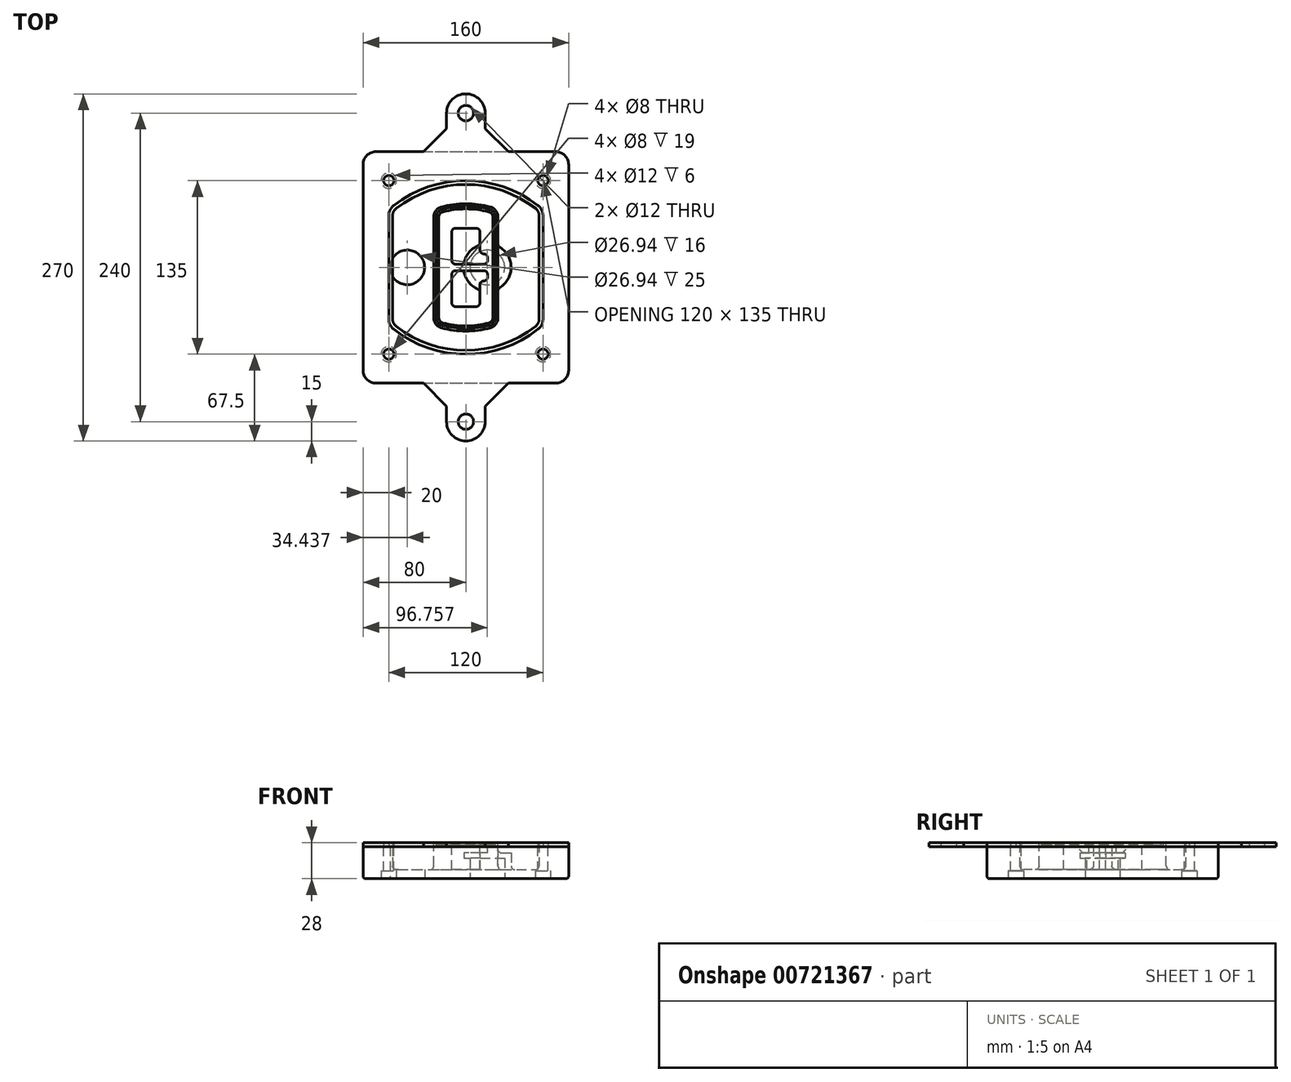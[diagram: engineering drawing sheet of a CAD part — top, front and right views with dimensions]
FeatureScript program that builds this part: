
annotation { "Feature Type Name" : "Feature", "Feature Type Description" : "" }
export const myFeature = defineFeature(function(context is Context, id is Id, definition is map)
    precondition{}
    {
        {
            var Q0;
            Q0=qCreatedBy(makeId("Top.planeOp"),FACE);
            var sketch = newSketch(context, id + "F0", { "sketchPlane" : qUnion([Q0])});
            skPoint(sketch, "E0.rect.middle", {"position": v(0, 0) * mm});
            skLineSegment(sketch, "E1.bottom", {"start": v(-70, -90) * mm, "end": v(70, -90) * mm});
            skLineSegment(sketch, "E1.top", {"start": v(-70, 90) * mm, "end": v(70, 90) * mm});
            skLineSegment(sketch, "E1.left", {"start": v(-80, -80) * mm, "end": v(-80, 80) * mm});
            skLineSegment(sketch, "E1.right", {"start": v(80, -80) * mm, "end": v(80, 80) * mm});
            skLineSegment(sketch, "E2", {"start": v(-80, 90) * mm, "end": v(80, -90) * mm, "construction": true});
            skLineSegment(sketch, "E3", {"start": v(80, 90) * mm, "end": v(-80, -90) * mm, "construction": true});
            skCircle(sketch, "E4", {"center": v(-60, 67.5) * mm, "radius": 4 * mm});
            skCircle(sketch, "E5", {"center": v(60, 67.5) * mm, "radius": 4 * mm});
            skCircle(sketch, "E6", {"center": v(60, -67.5) * mm, "radius": 4 * mm});
            skCircle(sketch, "E7", {"center": v(-60, -67.5) * mm, "radius": 4 * mm});
            skLineSegment(sketch, "E8", {"start": v(-60, 67.5) * mm, "end": v(60, 67.5) * mm, "construction": true});
            skLineSegment(sketch, "E9", {"start": v(60, 67.5) * mm, "end": v(60, -67.5) * mm, "construction": true});
            skLineSegment(sketch, "E10", {"start": v(60, -67.5) * mm, "end": v(-60, -67.5) * mm, "construction": true});
            skLineSegment(sketch, "E11", {"start": v(-60, -67.5) * mm, "end": v(-60, 67.5) * mm, "construction": true});
            skLineSegment(sketch, "E12", {"start": v(-60, 40.3) * mm, "end": v(-60, -40.3) * mm});
            skLineSegment(sketch, "E13", {"start": v(60, 40.3) * mm, "end": v(60, -40.3) * mm});
            skArc(sketch, "E14", {"start": v(56.15, 48.18) * mm, "mid": v(0, 67.5) * mm, "end": v(-56.15, 48.18) * mm});
            skArc(sketch, "E15", {"start": v(-56.15, -48.18) * mm, "mid": v(0, -67.5) * mm, "end": v(56.15, -48.18) * mm});
            skLineSegment(sketch, "E16", {"start": v(-60, 0) * mm, "end": v(60, 0) * mm, "construction": true});
            skPoint(sketch, "E17.visualSharp", {"position": v(-60, -45) * mm});
            skArc(sketch, "E17.filletArc", {"start": v(-60, -40.3) * mm, "mid": v(-58.99, -44.68) * mm, "end": v(-56.15, -48.18) * mm});
            skPoint(sketch, "E18.visualSharp", {"position": v(-60, 45) * mm});
            skArc(sketch, "E18.filletArc", {"start": v(-56.15, 48.18) * mm, "mid": v(-58.99, 44.68) * mm, "end": v(-60, 40.3) * mm});
            skPoint(sketch, "E19.visualSharp", {"position": v(60, 45) * mm});
            skArc(sketch, "E19.filletArc", {"start": v(60, 40.3) * mm, "mid": v(58.99, 44.68) * mm, "end": v(56.15, 48.18) * mm});
            skPoint(sketch, "E20.visualSharp", {"position": v(60, -45) * mm});
            skArc(sketch, "E20.filletArc", {"start": v(56.15, -48.18) * mm, "mid": v(58.99, -44.68) * mm, "end": v(60, -40.3) * mm});
            skPoint(sketch, "E21.visualSharp", {"position": v(-80, 90) * mm});
            skArc(sketch, "E21.filletArc", {"start": v(-70, 90) * mm, "mid": v(-77.07, 87.07) * mm, "end": v(-80, 80) * mm});
            skPoint(sketch, "E22.visualSharp", {"position": v(80, 90) * mm});
            skArc(sketch, "E22.filletArc", {"start": v(80, 80) * mm, "mid": v(77.07, 87.07) * mm, "end": v(70, 90) * mm});
            skPoint(sketch, "E23.visualSharp", {"position": v(80, -90) * mm});
            skArc(sketch, "E23.filletArc", {"start": v(70, -90) * mm, "mid": v(77.07, -87.07) * mm, "end": v(80, -80) * mm});
            skPoint(sketch, "E24.visualSharp", {"position": v(-80, -90) * mm});
            skArc(sketch, "E24.filletArc", {"start": v(-80, -80) * mm, "mid": v(-77.07, -87.07) * mm, "end": v(-70, -90) * mm});
            skArc(sketch, "E25.0", {"start": v(57, 40.3) * mm, "mid": v(56.3, 43.36) * mm, "end": v(54.3, 45.81) * mm});
            skLineSegment(sketch, "E25.1", {"start": v(57, 40.3) * mm, "end": v(57, -40.3) * mm});
            skArc(sketch, "E25.2", {"start": v(54.3, -45.81) * mm, "mid": v(56.3, -43.36) * mm, "end": v(57, -40.3) * mm});
            skArc(sketch, "E25.3", {"start": v(-54.3, -45.81) * mm, "mid": v(0, -64.5) * mm, "end": v(54.3, -45.81) * mm});
            skArc(sketch, "E25.4", {"start": v(-57, -40.3) * mm, "mid": v(-56.3, -43.36) * mm, "end": v(-54.3, -45.81) * mm});
            skArc(sketch, "E25.5", {"start": v(54.3, 45.81) * mm, "mid": v(0, 64.5) * mm, "end": v(-54.3, 45.81) * mm});
            skLineSegment(sketch, "E25.6", {"start": v(-57, 40.3) * mm, "end": v(-57, -40.3) * mm});
            skArc(sketch, "E25.7", {"start": v(-54.3, 45.81) * mm, "mid": v(-56.3, 43.36) * mm, "end": v(-57, 40.3) * mm});
            skArc(sketch, "E26.0", {"start": v(-58.62, 51.33) * mm, "mid": v(-62.58, 46.43) * mm, "end": v(-64, 40.3) * mm});
            skArc(sketch, "E26.1", {"start": v(58.62, 51.33) * mm, "mid": v(0, 71.5) * mm, "end": v(-58.62, 51.33) * mm});
            skArc(sketch, "E26.2", {"start": v(64, 40.3) * mm, "mid": v(62.58, 46.43) * mm, "end": v(58.62, 51.33) * mm});
            skLineSegment(sketch, "E26.3", {"start": v(64, 40.3) * mm, "end": v(64, -40.3) * mm});
            skArc(sketch, "E26.4", {"start": v(58.62, -51.33) * mm, "mid": v(62.58, -46.43) * mm, "end": v(64, -40.3) * mm});
            skLineSegment(sketch, "E26.5", {"start": v(-64, 40.3) * mm, "end": v(-64, -40.3) * mm});
            skArc(sketch, "E26.6", {"start": v(-58.62, -51.33) * mm, "mid": v(0, -71.5) * mm, "end": v(58.62, -51.33) * mm});
            skArc(sketch, "E26.7", {"start": v(-64, -40.3) * mm, "mid": v(-62.58, -46.43) * mm, "end": v(-58.62, -51.33) * mm});
            skSolve(sketch);
        }
        {
            var Q0;
            Q0=makeQuery(id+"F0.imprint","IMPRINT",FACE,{"disambiguationData":[TD([[makeQuery(id+"F0.imprint","IMPRINT",EDGE,{"derivedFrom":sQuery(id+"F0.wireOp",EDGE,"E1.bottom")}),1.0]])]});
            var Q1;
            Q1=makeQuery(id+"F0.imprint","IMPRINT",FACE,{"disambiguationData":[TD([[makeQuery(id+"F0.imprint","IMPRINT",EDGE,{"derivedFrom":sQuery(id+"F0.wireOp",EDGE,"E12")}),1.0]])]});
            var Q2;
            Q2=makeQuery(id+"F0.imprint","IMPRINT",FACE,{"disambiguationData":[TD([[makeQuery(id+"F0.imprint","IMPRINT",EDGE,{"derivedFrom":sQuery(id+"F0.wireOp",EDGE,"E25.0")}),1.0]])]});
            var Q3;
            Q3=makeQuery(id+"F0.imprint","IMPRINT",FACE,{"disambiguationData":[TD([[makeQuery(id+"F0.imprint","IMPRINT",EDGE,{"derivedFrom":sQuery(id+"F0.wireOp",EDGE,"E12")}),-1.0]])]});
            extrude(context, id + "F1", {"entities" : qUnion([Q0, Q1, Q2, Q3]), "oppositeDirection" : true, "depth" : 25 * mm});
        }
        {
            var Q0;
            Q0=makeQuery(id+"F0.imprint","IMPRINT",FACE,{"disambiguationData":[TD([[makeQuery(id+"F0.imprint","IMPRINT",EDGE,{"derivedFrom":sQuery(id+"F0.wireOp",EDGE,"E12")}),1.0]])]});
            extrude(context, id + "F2", {"entities" : qUnion([Q0]), "operationType" : NewBodyOperationType.ADD, "depth" : 3 * mm});
        }
        {
            var Q0;
            Q0=makeQuery(id+"F0.imprint","IMPRINT",FACE,{"disambiguationData":[TD([[makeQuery(id+"F0.imprint","IMPRINT",EDGE,{"derivedFrom":sQuery(id+"F0.wireOp",EDGE,"E25.0")}),1.0]])]});
            extrude(context, id + "F3", {"entities" : qUnion([Q0]), "operationType" : NewBodyOperationType.REMOVE, "oppositeDirection" : true, "depth" : 18 * mm});
        }
        {
            var Q0;
            Q0=makeQuery(id+"F2.opExtrude","CAP_FACE",FACE,{"disambiguationData":[OSD([sQuery(id+"F0.wireOp",EDGE,"E12"),sQuery(id+"F0.wireOp",EDGE,"E13"),sQuery(id+"F0.wireOp",EDGE,"E14"),sQuery(id+"F0.wireOp",EDGE,"E15"),sQuery(id+"F0.wireOp",EDGE,"E17.filletArc"),sQuery(id+"F0.wireOp",EDGE,"E18.filletArc"),sQuery(id+"F0.wireOp",EDGE,"E19.filletArc"),sQuery(id+"F0.wireOp",EDGE,"E20.filletArc"),sQuery(id+"F0.wireOp",EDGE,"E25.0"),sQuery(id+"F0.wireOp",EDGE,"E25.1"),sQuery(id+"F0.wireOp",EDGE,"E25.2"),sQuery(id+"F0.wireOp",EDGE,"E25.3"),sQuery(id+"F0.wireOp",EDGE,"E25.4"),sQuery(id+"F0.wireOp",EDGE,"E25.5"),sQuery(id+"F0.wireOp",EDGE,"E25.6"),sQuery(id+"F0.wireOp",EDGE,"E25.7")])],"isStart":false});
            var sketch = newSketch(context, id + "F4", { "sketchPlane" : qUnion([Q0])});
            skArc(sketch, "E27.0", {"start": v(-19.08, -46.97) * mm, "mid": v(0, -49.5) * mm, "end": v(19.08, -46.97) * mm});
            skArc(sketch, "E28.0", {"start": v(19.08, 46.97) * mm, "mid": v(0, 49.5) * mm, "end": v(-19.08, 46.97) * mm});
            skLineSegment(sketch, "E29", {"start": v(-25, 39.25) * mm, "end": v(-25, -39.25) * mm});
            skLineSegment(sketch, "E30", {"start": v(25, 39.25) * mm, "end": v(25, -39.25) * mm});
            skLineSegment(sketch, "E31", {"start": v(-25, 45.1) * mm, "end": v(25, 45.1) * mm, "construction": true});
            skLineSegment(sketch, "E32", {"start": v(-25, -45.1) * mm, "end": v(25, -45.1) * mm, "construction": true});
            skPoint(sketch, "E33.visualSharp", {"position": v(-25, 45.1) * mm});
            skArc(sketch, "E33.filletArc", {"start": v(-19.08, 46.97) * mm, "mid": v(-23.35, 44.11) * mm, "end": v(-25, 39.25) * mm});
            skPoint(sketch, "E34.visualSharp", {"position": v(25, 45.1) * mm});
            skArc(sketch, "E34.filletArc", {"start": v(25, 39.25) * mm, "mid": v(23.35, 44.11) * mm, "end": v(19.08, 46.97) * mm});
            skPoint(sketch, "E35.visualSharp", {"position": v(25, -45.1) * mm});
            skArc(sketch, "E35.filletArc", {"start": v(19.08, -46.97) * mm, "mid": v(23.35, -44.11) * mm, "end": v(25, -39.25) * mm});
            skPoint(sketch, "E36.visualSharp", {"position": v(-25, -45.1) * mm});
            skArc(sketch, "E36.filletArc", {"start": v(-25, -39.25) * mm, "mid": v(-23.35, -44.11) * mm, "end": v(-19.08, -46.97) * mm});
            skArc(sketch, "E37.0", {"start": v(54.3, 45.81) * mm, "mid": v(0, 64.5) * mm, "end": v(-54.3, 45.81) * mm});
            skArc(sketch, "E37.1", {"start": v(-54.3, 45.81) * mm, "mid": v(-56.3, 43.36) * mm, "end": v(-57, 40.3) * mm});
            skLineSegment(sketch, "E37.2", {"start": v(-57, 40.3) * mm, "end": v(-57, -40.3) * mm});
            skArc(sketch, "E37.3", {"start": v(-57, -40.3) * mm, "mid": v(-56.3, -43.36) * mm, "end": v(-54.3, -45.81) * mm});
            skArc(sketch, "E37.4", {"start": v(-54.3, -45.81) * mm, "mid": v(0, -64.5) * mm, "end": v(54.3, -45.81) * mm});
            skArc(sketch, "E37.5", {"start": v(54.3, -45.81) * mm, "mid": v(56.3, -43.36) * mm, "end": v(57, -40.3) * mm});
            skLineSegment(sketch, "E37.6", {"start": v(57, 40.3) * mm, "end": v(57, -40.3) * mm});
            skArc(sketch, "E37.7", {"start": v(57, 40.3) * mm, "mid": v(56.3, 43.36) * mm, "end": v(54.3, 45.81) * mm});
            skLineSegment(sketch, "E38.0", {"start": v(23, 39.25) * mm, "end": v(23, -39.25) * mm});
            skArc(sketch, "E38.1", {"start": v(18.56, -45.04) * mm, "mid": v(21.76, -42.9) * mm, "end": v(23, -39.25) * mm});
            skArc(sketch, "E38.2", {"start": v(-18.56, -45.04) * mm, "mid": v(0, -47.5) * mm, "end": v(18.56, -45.04) * mm});
            skArc(sketch, "E38.3", {"start": v(-23, -39.25) * mm, "mid": v(-21.76, -42.9) * mm, "end": v(-18.56, -45.04) * mm});
            skLineSegment(sketch, "E38.4", {"start": v(-23, 39.25) * mm, "end": v(-23, -39.25) * mm});
            skArc(sketch, "E38.5", {"start": v(23, 39.25) * mm, "mid": v(21.76, 42.9) * mm, "end": v(18.56, 45.04) * mm});
            skArc(sketch, "E38.6", {"start": v(-18.56, 45.04) * mm, "mid": v(-21.76, 42.9) * mm, "end": v(-23, 39.25) * mm});
            skArc(sketch, "E38.7", {"start": v(18.56, 45.04) * mm, "mid": v(0, 47.5) * mm, "end": v(-18.56, 45.04) * mm});
            skArc(sketch, "E39.0", {"start": v(21, 39.25) * mm, "mid": v(20.18, 41.68) * mm, "end": v(18.04, 43.1) * mm});
            skLineSegment(sketch, "E39.1", {"start": v(21, 39.25) * mm, "end": v(21, -39.25) * mm});
            skArc(sketch, "E39.2", {"start": v(18.04, -43.1) * mm, "mid": v(20.18, -41.68) * mm, "end": v(21, -39.25) * mm});
            skArc(sketch, "E39.3", {"start": v(-18.04, -43.1) * mm, "mid": v(0, -45.5) * mm, "end": v(18.04, -43.1) * mm});
            skArc(sketch, "E39.4", {"start": v(-21, -39.25) * mm, "mid": v(-20.18, -41.68) * mm, "end": v(-18.04, -43.1) * mm});
            skArc(sketch, "E39.5", {"start": v(18.04, 43.1) * mm, "mid": v(0, 45.5) * mm, "end": v(-18.04, 43.1) * mm});
            skLineSegment(sketch, "E39.6", {"start": v(-21, 39.25) * mm, "end": v(-21, -39.25) * mm});
            skArc(sketch, "E39.7", {"start": v(-18.04, 43.1) * mm, "mid": v(-20.18, 41.68) * mm, "end": v(-21, 39.25) * mm});
            skLineSegment(sketch, "E40", {"start": v(-25, 0) * mm, "end": v(25, 0) * mm, "construction": true});
            skLineSegment(sketch, "E41", {"start": v(-11, 5.5) * mm, "end": v(-11, 27.5) * mm});
            skLineSegment(sketch, "E42", {"start": v(-8, 30.5) * mm, "end": v(8, 30.5) * mm});
            skLineSegment(sketch, "E43", {"start": v(11, 27.5) * mm, "end": v(11, 13.5) * mm});
            skLineSegment(sketch, "E44", {"start": v(14, 10.5) * mm, "end": v(14, 10.5) * mm});
            skLineSegment(sketch, "E45", {"start": v(17, 7.5) * mm, "end": v(17, 5.5) * mm});
            skLineSegment(sketch, "E46", {"start": v(14, 2.5) * mm, "end": v(-8, 2.5) * mm});
            skPoint(sketch, "E47.visualSharp", {"position": v(-11, 30.5) * mm});
            skArc(sketch, "E47.filletArc", {"start": v(-8, 30.5) * mm, "mid": v(-10.12, 29.62) * mm, "end": v(-11, 27.5) * mm});
            skPoint(sketch, "E48.visualSharp", {"position": v(11, 30.5) * mm});
            skArc(sketch, "E48.filletArc", {"start": v(11, 27.5) * mm, "mid": v(10.12, 29.62) * mm, "end": v(8, 30.5) * mm});
            skPoint(sketch, "E49.visualSharp", {"position": v(11, 10.5) * mm});
            skArc(sketch, "E49.filletArc", {"start": v(11, 13.5) * mm, "mid": v(11.88, 11.38) * mm, "end": v(14, 10.5) * mm});
            skPoint(sketch, "E50.visualSharp", {"position": v(17, 10.5) * mm});
            skArc(sketch, "E50.filletArc", {"start": v(17, 7.5) * mm, "mid": v(16.12, 9.62) * mm, "end": v(14, 10.5) * mm});
            skPoint(sketch, "E51.visualSharp", {"position": v(17, 2.5) * mm});
            skArc(sketch, "E51.filletArc", {"start": v(14, 2.5) * mm, "mid": v(16.12, 3.38) * mm, "end": v(17, 5.5) * mm});
            skPoint(sketch, "E52.visualSharp", {"position": v(-11, 2.5) * mm});
            skArc(sketch, "E52.filletArc", {"start": v(-11, 5.5) * mm, "mid": v(-10.12, 3.38) * mm, "end": v(-8, 2.5) * mm});
            skLineSegment(sketch, "E53.0.MirrorCS", {"start": v(14, -2.5) * mm, "end": v(-8, -2.5) * mm});
            skArc(sketch, "E54.0.MirrorCS", {"start": v(-11, -5.5) * mm, "mid": v(-10.12, -3.38) * mm, "end": v(-8, -2.5) * mm});
            skLineSegment(sketch, "E55.0.MirrorCS", {"start": v(-11, -5.5) * mm, "end": v(-11, -27.5) * mm});
            skArc(sketch, "E56.0.MirrorCS", {"start": v(-8, -30.5) * mm, "mid": v(-10.12, -29.62) * mm, "end": v(-11, -27.5) * mm});
            skLineSegment(sketch, "E57.0.MirrorCS", {"start": v(-8, -30.5) * mm, "end": v(8, -30.5) * mm});
            skArc(sketch, "E58.0.MirrorCS", {"start": v(11, -27.5) * mm, "mid": v(10.12, -29.62) * mm, "end": v(8, -30.5) * mm});
            skLineSegment(sketch, "E59.0.MirrorCS", {"start": v(11, -27.5) * mm, "end": v(11, -13.5) * mm});
            skArc(sketch, "E60.0.MirrorCS", {"start": v(11, -13.5) * mm, "mid": v(11.88, -11.38) * mm, "end": v(14, -10.5) * mm});
            skArc(sketch, "E61.0.MirrorCS", {"start": v(17, -7.5) * mm, "mid": v(16.12, -9.62) * mm, "end": v(14, -10.5) * mm});
            skLineSegment(sketch, "E62.0.MirrorCS", {"start": v(17, -7.5) * mm, "end": v(17, -5.5) * mm});
            skArc(sketch, "E63.0.MirrorCS", {"start": v(14, -2.5) * mm, "mid": v(16.12, -3.38) * mm, "end": v(17, -5.5) * mm});
            skSolve(sketch);
        }
        {
            var Q0;
            Q0=makeQuery(id+"F4.imprint","IMPRINT",FACE,{"disambiguationData":[TD([[makeQuery(id+"F4.imprint","IMPRINT",EDGE,{"derivedFrom":sQuery(id+"F4.wireOp",EDGE,"E27.0")}),1.0]])]});
            var Q1;
            Q1=makeQuery(id+"F4.imprint","IMPRINT",FACE,{"disambiguationData":[TD([[makeQuery(id+"F4.imprint","IMPRINT",EDGE,{"derivedFrom":sQuery(id+"F4.wireOp",EDGE,"E38.0")}),-1.0]])]});
            var Q2;
            Q2=makeQuery(id+"F4.imprint","IMPRINT",FACE,{"disambiguationData":[TD([[makeQuery(id+"F4.imprint","IMPRINT",EDGE,{"derivedFrom":sQuery(id+"F4.wireOp",EDGE,"E39.0")}),1.0]])]});
            extrude(context, id + "F5", {"entities" : qUnion([Q0, Q1, Q2]), "operationType" : NewBodyOperationType.ADD, "endBound" : BoundingType.UP_TO_NEXT, "oppositeDirection" : true, "depth" : 25 * mm});
        }
        {
            var Q0;
            Q0=makeQuery(id+"F4.imprint","IMPRINT",FACE,{"disambiguationData":[TD([[makeQuery(id+"F4.imprint","IMPRINT",EDGE,{"derivedFrom":sQuery(id+"F4.wireOp",EDGE,"E38.0")}),-1.0]])]});
            extrude(context, id + "F6", {"entities" : qUnion([Q0]), "operationType" : NewBodyOperationType.REMOVE, "oppositeDirection" : true, "depth" : 2 * mm});
        }
        {
            var Q0;
            Q0=makeQuery(id+"F1.opExtrude","CAP_FACE",FACE,{"disambiguationData":[OSD([sQuery(id+"F0.wireOp",EDGE,"E1.bottom"),sQuery(id+"F0.wireOp",EDGE,"E1.top"),sQuery(id+"F0.wireOp",EDGE,"E1.left"),sQuery(id+"F0.wireOp",EDGE,"E1.right"),sQuery(id+"F0.wireOp",EDGE,"E4"),sQuery(id+"F0.wireOp",EDGE,"E5"),sQuery(id+"F0.wireOp",EDGE,"E6"),sQuery(id+"F0.wireOp",EDGE,"E7"),sQuery(id+"F0.wireOp",EDGE,"E21.filletArc"),sQuery(id+"F0.wireOp",EDGE,"E22.filletArc"),sQuery(id+"F0.wireOp",EDGE,"E23.filletArc"),sQuery(id+"F0.wireOp",EDGE,"E24.filletArc")])],"isStart":false});
            var sketch = newSketch(context, id + "F7", { "sketchPlane" : qUnion([Q0])});
            skCircle(sketch, "E64", {"center": v(16.76, 0) * mm, "radius": 13.47 * mm});
            skCircle(sketch, "E65", {"center": v(-45.56, 0) * mm, "radius": 13.47 * mm});
            skLineSegment(sketch, "E66", {"start": v(80, 0) * mm, "end": v(-80, 0) * mm});
            skCircle(sketch, "E67", {"center": v(16.76, 0) * mm, "radius": 18.47 * mm});
            skCircle(sketch, "E68", {"center": v(60, -67.5) * mm, "radius": 6 * mm});
            skCircle(sketch, "E69", {"center": v(-60, -67.5) * mm, "radius": 6 * mm});
            skCircle(sketch, "E70", {"center": v(-60, 67.5) * mm, "radius": 6 * mm});
            skCircle(sketch, "E71", {"center": v(60, 67.5) * mm, "radius": 6 * mm});
            skSolve(sketch);
        }
        {
            var Q0;
            {var subQ1=sQuery(id+"F7.wireOp",EDGE,"E66");var subQ4=sQuery(id+"F7.wireOp",EDGE,"E64");var subQ6=makeQuery(id+"F7.imprint","INTERSECT",VERTEX,{"disambiguationData":[OD(0.0)],"derivedFrom":[subQ4,subQ1]});Q0=makeQuery(id+"F7.imprint","IMPRINT",FACE,{"disambiguationData":[TD([[makeQuery(id+"F7.imprint","IMPRINT",EDGE,{"disambiguationData":[TD([[subQ6,-1.0]])],"derivedFrom":subQ4}),-1.0]])]});}
            var Q1;
            {var subQ0=sQuery(id+"F7.wireOp",EDGE,"E66");var subQ1=sQuery(id+"F7.wireOp",EDGE,"E64");var subQ3=makeQuery(id+"F7.imprint","INTERSECT",VERTEX,{"disambiguationData":[OD(0.0)],"derivedFrom":[subQ1,subQ0]});Q1=makeQuery(id+"F7.imprint","IMPRINT",FACE,{"disambiguationData":[TD([[makeQuery(id+"F7.imprint","IMPRINT",EDGE,{"disambiguationData":[TD([[subQ3,-1.0]])],"derivedFrom":subQ1}),1.0]])]});}
            var Q2;
            {var subQ0=sQuery(id+"F7.wireOp",EDGE,"E66");var subQ1=sQuery(id+"F7.wireOp",EDGE,"E64");var subQ3=makeQuery(id+"F7.imprint","INTERSECT",VERTEX,{"disambiguationData":[OD(0.0)],"derivedFrom":[subQ1,subQ0]});Q2=makeQuery(id+"F7.imprint","IMPRINT",FACE,{"disambiguationData":[TD([[makeQuery(id+"F7.imprint","IMPRINT",EDGE,{"disambiguationData":[TD([[subQ3,1.0]])],"derivedFrom":subQ1}),1.0]])]});}
            var Q3;
            {var subQ1=sQuery(id+"F7.wireOp",EDGE,"E66");var subQ4=sQuery(id+"F7.wireOp",EDGE,"E64");var subQ6=makeQuery(id+"F7.imprint","INTERSECT",VERTEX,{"disambiguationData":[OD(0.0)],"derivedFrom":[subQ4,subQ1]});Q3=makeQuery(id+"F7.imprint","IMPRINT",FACE,{"disambiguationData":[TD([[makeQuery(id+"F7.imprint","IMPRINT",EDGE,{"disambiguationData":[TD([[subQ6,1.0]])],"derivedFrom":subQ4}),-1.0]])]});}
            extrude(context, id + "F8", {"entities" : qUnion([Q0, Q1, Q2, Q3]), "operationType" : NewBodyOperationType.ADD, "oppositeDirection" : true, "depth" : 20 * mm});
        }
        {
            var Q0;
            {var subQ0=sQuery(id+"F7.wireOp",EDGE,"E66");var subQ1=sQuery(id+"F7.wireOp",EDGE,"E64");var subQ3=makeQuery(id+"F7.imprint","INTERSECT",VERTEX,{"disambiguationData":[OD(0.0)],"derivedFrom":[subQ1,subQ0]});Q0=makeQuery(id+"F7.imprint","IMPRINT",FACE,{"disambiguationData":[TD([[makeQuery(id+"F7.imprint","IMPRINT",EDGE,{"disambiguationData":[TD([[subQ3,-1.0]])],"derivedFrom":subQ1}),1.0]])]});}
            var Q1;
            {var subQ0=sQuery(id+"F7.wireOp",EDGE,"E66");var subQ1=sQuery(id+"F7.wireOp",EDGE,"E64");var subQ3=makeQuery(id+"F7.imprint","INTERSECT",VERTEX,{"disambiguationData":[OD(0.0)],"derivedFrom":[subQ1,subQ0]});Q1=makeQuery(id+"F7.imprint","IMPRINT",FACE,{"disambiguationData":[TD([[makeQuery(id+"F7.imprint","IMPRINT",EDGE,{"disambiguationData":[TD([[subQ3,1.0]])],"derivedFrom":subQ1}),1.0]])]});}
            extrude(context, id + "F9", {"entities" : qUnion([Q0, Q1]), "operationType" : NewBodyOperationType.REMOVE, "oppositeDirection" : true, "depth" : 16 * mm});
        }
        {
            var Q0;
            {var subQ0=sQuery(id+"F7.wireOp",EDGE,"E66");var subQ1=sQuery(id+"F7.wireOp",EDGE,"E65");var subQ3=makeQuery(id+"F7.imprint","INTERSECT",VERTEX,{"disambiguationData":[OD(0.0)],"derivedFrom":[subQ1,subQ0]});Q0=makeQuery(id+"F7.imprint","IMPRINT",FACE,{"disambiguationData":[TD([[makeQuery(id+"F7.imprint","IMPRINT",EDGE,{"disambiguationData":[TD([[subQ3,-1.0]])],"derivedFrom":subQ1}),1.0]])]});}
            var Q1;
            {var subQ0=sQuery(id+"F7.wireOp",EDGE,"E66");var subQ1=sQuery(id+"F7.wireOp",EDGE,"E65");var subQ3=makeQuery(id+"F7.imprint","INTERSECT",VERTEX,{"disambiguationData":[OD(0.0)],"derivedFrom":[subQ1,subQ0]});Q1=makeQuery(id+"F7.imprint","IMPRINT",FACE,{"disambiguationData":[TD([[makeQuery(id+"F7.imprint","IMPRINT",EDGE,{"disambiguationData":[TD([[subQ3,1.0]])],"derivedFrom":subQ1}),1.0]])]});}
            extrude(context, id + "F10", {"entities" : qUnion([Q0, Q1]), "operationType" : NewBodyOperationType.REMOVE, "oppositeDirection" : true, "depth" : 25 * mm});
        }
        {
            var Q0;
            Q0=makeQuery(id+"F7.imprint","IMPRINT",FACE,{"disambiguationData":[TD([[makeQuery(id+"F7.imprint","IMPRINT",EDGE,{"derivedFrom":sQuery(id+"F7.wireOp",EDGE,"E68")}),1.0]])]});
            var Q1;
            Q1=makeQuery(id+"F7.imprint","IMPRINT",FACE,{"disambiguationData":[TD([[makeQuery(id+"F7.imprint","IMPRINT",EDGE,{"derivedFrom":makeQuery(id+"F1.opExtrude","CAP_EDGE",EDGE,{"disambiguationData":[OSD([sQuery(id+"F0.wireOp",EDGE,"E5")])],"isStart":false})}),-1.0]])]});
            var Q2;
            Q2=makeQuery(id+"F7.imprint","IMPRINT",FACE,{"disambiguationData":[TD([[makeQuery(id+"F7.imprint","IMPRINT",EDGE,{"derivedFrom":sQuery(id+"F7.wireOp",EDGE,"E69")}),1.0]])]});
            var Q3;
            Q3=makeQuery(id+"F7.imprint","IMPRINT",FACE,{"disambiguationData":[TD([[makeQuery(id+"F7.imprint","IMPRINT",EDGE,{"derivedFrom":makeQuery(id+"F1.opExtrude","CAP_EDGE",EDGE,{"disambiguationData":[OSD([sQuery(id+"F0.wireOp",EDGE,"E4")])],"isStart":false})}),-1.0]])]});
            var Q4;
            Q4=makeQuery(id+"F7.imprint","IMPRINT",FACE,{"disambiguationData":[TD([[makeQuery(id+"F7.imprint","IMPRINT",EDGE,{"derivedFrom":sQuery(id+"F7.wireOp",EDGE,"E70")}),1.0]])]});
            var Q5;
            Q5=makeQuery(id+"F7.imprint","IMPRINT",FACE,{"disambiguationData":[TD([[makeQuery(id+"F7.imprint","IMPRINT",EDGE,{"derivedFrom":makeQuery(id+"F1.opExtrude","CAP_EDGE",EDGE,{"disambiguationData":[OSD([sQuery(id+"F0.wireOp",EDGE,"E7")])],"isStart":false})}),-1.0]])]});
            var Q6;
            Q6=makeQuery(id+"F7.imprint","IMPRINT",FACE,{"disambiguationData":[TD([[makeQuery(id+"F7.imprint","IMPRINT",EDGE,{"derivedFrom":sQuery(id+"F7.wireOp",EDGE,"E71")}),1.0]])]});
            var Q7;
            Q7=makeQuery(id+"F7.imprint","IMPRINT",FACE,{"disambiguationData":[TD([[makeQuery(id+"F7.imprint","IMPRINT",EDGE,{"derivedFrom":makeQuery(id+"F1.opExtrude","CAP_EDGE",EDGE,{"disambiguationData":[OSD([sQuery(id+"F0.wireOp",EDGE,"E6")])],"isStart":false})}),-1.0]])]});
            extrude(context, id + "F11", {"entities" : qUnion([Q0, Q1, Q2, Q3, Q4, Q5, Q6, Q7]), "operationType" : NewBodyOperationType.REMOVE, "oppositeDirection" : true, "depth" : 6 * mm});
        }
        {
            var Q0;
            Q0=makeQuery(id+"F9.boolean.opBoolean","COPY",FACE,{"derivedFrom":makeQuery(id+"F9.opExtrude","CAP_FACE",FACE,{"disambiguationData":[OSD([sQuery(id+"F7.wireOp",EDGE,"E64")])],"isStart":false})});
            var sketch = newSketch(context, id + "F12", { "sketchPlane" : qUnion([Q0])});
            skArc(sketch, "E72.0", {"start": v(11, 17.55) * mm, "mid": v(2.57, 11.82) * mm, "end": v(-1.54, 2.5) * mm});
            skArc(sketch, "E72.1", {"start": v(-1.54, -2.5) * mm, "mid": v(2.57, -11.82) * mm, "end": v(11, -17.55) * mm});
            skLineSegment(sketch, "E73", {"start": v(-1.54, -2.5) * mm, "end": v(14, -2.5) * mm});
            skLineSegment(sketch, "E74.0", {"start": v(14, 2.5) * mm, "end": v(-1.54, 2.5) * mm});
            skArc(sketch, "E74.1", {"start": v(14, 2.5) * mm, "mid": v(16.12, 3.38) * mm, "end": v(17, 5.5) * mm});
            skLineSegment(sketch, "E74.2", {"start": v(17, 7.5) * mm, "end": v(17, 5.5) * mm});
            skArc(sketch, "E74.3", {"start": v(17, 7.5) * mm, "mid": v(16.12, 9.62) * mm, "end": v(14, 10.5) * mm});
            skArc(sketch, "E74.4", {"start": v(11, 13.5) * mm, "mid": v(11.88, 11.38) * mm, "end": v(14, 10.5) * mm});
            skLineSegment(sketch, "E74.5", {"start": v(11, 17.55) * mm, "end": v(11, 13.5) * mm});
            skLineSegment(sketch, "E74.7", {"start": v(14, -2.5) * mm, "end": v(-1.54, -2.5) * mm});
            skArc(sketch, "E74.8", {"start": v(14, -2.5) * mm, "mid": v(16.12, -3.38) * mm, "end": v(17, -5.5) * mm});
            skLineSegment(sketch, "E74.9", {"start": v(17, -7.5) * mm, "end": v(17, -5.5) * mm});
            skArc(sketch, "E74.10", {"start": v(17, -7.5) * mm, "mid": v(16.12, -9.62) * mm, "end": v(14, -10.5) * mm});
            skArc(sketch, "E74.11", {"start": v(11, -13.5) * mm, "mid": v(11.88, -11.38) * mm, "end": v(14, -10.5) * mm});
            skLineSegment(sketch, "E74.12", {"start": v(11, -17.55) * mm, "end": v(11, -13.5) * mm});
            skPoint(sketch, "E75.orphan", {"position": v(11, -27.5) * mm});
            skPoint(sketch, "E76.orphan", {"position": v(-8, -2.5) * mm});
            skPoint(sketch, "E77.orphan", {"position": v(-8, 2.5) * mm});
            skPoint(sketch, "E78.orphan", {"position": v(11, 27.5) * mm});
            skSolve(sketch);
        }
        {
            var Q0;
            {var subQ7=sQuery(id+"F12.wireOp",EDGE,"E72.0");var subQ14=sQuery(id+"F12.wireOp",EDGE,"E72.1");var subQ16=sQuery(id+"F12.wireOp",EDGE,"E74.1");var subQ18=sQuery(id+"F12.wireOp",EDGE,"E74.8");Q0=qUnion([makeQuery(id+"F12.imprint","IMPRINT",FACE,{"disambiguationData":[TD([[makeQuery(id+"F12.imprint","IMPRINT",EDGE,{"derivedFrom":subQ7}),1.0]])]}),makeQuery(id+"F12.imprint","IMPRINT",FACE,{"disambiguationData":[TD([[makeQuery(id+"F12.imprint","IMPRINT",EDGE,{"derivedFrom":subQ14}),1.0]])]}),makeQuery(id+"F12.imprint","IMPRINT",FACE,{"disambiguationData":[TD([[makeQuery(id+"F12.imprint","IMPRINT",EDGE,{"derivedFrom":subQ16}),1.0]])]}),makeQuery(id+"F12.imprint","IMPRINT",FACE,{"disambiguationData":[TD([[makeQuery(id+"F12.imprint","IMPRINT",EDGE,{"derivedFrom":subQ18}),-1.0]])]})]);}
            var Q1;
            Q1=makeQuery(id+"F5.boolean.opBoolean","SPLIT",FACE,{"disambiguationData":[TD([makeQuery(id+"F5.opExtrude","SWEPT_FACE",FACE,{"disambiguationData":[OSD([sQuery(id+"F4.wireOp",EDGE,"E41")])]})])],"derivedFrom":makeQuery(id+"F3.boolean.opBoolean","COPY",FACE,{"derivedFrom":makeQuery(id+"F3.opExtrude","CAP_FACE",FACE,{"disambiguationData":[OSD([sQuery(id+"F0.wireOp",EDGE,"E25.0"),sQuery(id+"F0.wireOp",EDGE,"E25.1"),sQuery(id+"F0.wireOp",EDGE,"E25.2"),sQuery(id+"F0.wireOp",EDGE,"E25.3"),sQuery(id+"F0.wireOp",EDGE,"E25.4"),sQuery(id+"F0.wireOp",EDGE,"E25.5"),sQuery(id+"F0.wireOp",EDGE,"E25.6"),sQuery(id+"F0.wireOp",EDGE,"E25.7")])],"isStart":false})})});
            extrude(context, id + "F13", {"entities" : qUnion([Q0]), "operationType" : NewBodyOperationType.REMOVE, "endBound" : BoundingType.UP_TO_SURFACE, "endBoundEntityFace" : qUnion([Q1]), "depth" : 25 * mm});
        }
        {
            var Q0;
            Q0=makeQuery(id+"F3.boolean.opBoolean","COPY",EDGE,{"derivedFrom":makeQuery(id+"F3.opExtrude","CAP_EDGE",EDGE,{"disambiguationData":[OSD([sQuery(id+"F0.wireOp",EDGE,"E25.6")])],"isStart":false})});
            var Q1;
            Q1=makeQuery(id+"F8.boolean.opBoolean","INTERSECT",EDGE,{"derivedFrom":[makeQuery(id+"F5.opExtrude","SWEPT_FACE",FACE,{"disambiguationData":[OSD([sQuery(id+"F4.wireOp",EDGE,"E30")])]}),makeQuery(id+"F8.opExtrude","CAP_FACE",FACE,{"disambiguationData":[OSD([sQuery(id+"F7.wireOp",EDGE,"E67")])],"isStart":false})]});
            var Q2;
            Q2=makeQuery(id+"F8.boolean.opBoolean","INTERSECT",EDGE,{"disambiguationData":[OD(1.0)],"derivedFrom":[makeQuery(id+"F5.opExtrude","SWEPT_FACE",FACE,{"disambiguationData":[OSD([sQuery(id+"F4.wireOp",EDGE,"E30")])]}),makeQuery(id+"F8.opExtrude","SWEPT_FACE",FACE,{"disambiguationData":[OSD([sQuery(id+"F7.wireOp",EDGE,"E67")])]})]});
            var Q3;
            {var subQ0=sQuery(id+"F4.wireOp",EDGE,"E30");Q3=makeQuery(id+"F8.boolean.opBoolean","SPLIT",EDGE,{"disambiguationData":[TD([makeQuery(id+"F5.opExtrude","SWEPT_FACE",FACE,{"disambiguationData":[OSD([sQuery(id+"F4.wireOp",EDGE,"E35.filletArc")])]})])],"derivedFrom":makeQuery(id+"F5.opExtrude","CAP_EDGE",EDGE,{"disambiguationData":[OSD([subQ0])],"isStart":false})});}
            var Q4;
            {var subQ0=sQuery(id+"F0.wireOp",EDGE,"E25.7");var subQ1=sQuery(id+"F0.wireOp",EDGE,"E25.1");var subQ2=sQuery(id+"F0.wireOp",EDGE,"E25.6");var subQ3=sQuery(id+"F0.wireOp",EDGE,"E25.5");var subQ4=sQuery(id+"F0.wireOp",EDGE,"E25.4");var subQ5=sQuery(id+"F0.wireOp",EDGE,"E25.0");var subQ6=sQuery(id+"F0.wireOp",EDGE,"E25.2");var subQ7=sQuery(id+"F0.wireOp",EDGE,"E25.3");Q4=makeQuery(id+"F8.boolean.opBoolean","INTERSECT",EDGE,{"derivedFrom":[makeQuery(id+"F5.boolean.opBoolean","SPLIT",FACE,{"disambiguationData":[TD([makeQuery(id+"F2.opExtrude","SWEPT_FACE",FACE,{"disambiguationData":[OSD([subQ5])]})])],"derivedFrom":makeQuery(id+"F3.boolean.opBoolean","COPY",FACE,{"derivedFrom":makeQuery(id+"F3.opExtrude","CAP_FACE",FACE,{"disambiguationData":[OSD([subQ5,subQ1,subQ6,subQ7,subQ4,subQ3,subQ2,subQ0])],"isStart":false})})}),makeQuery(id+"F8.opExtrude","SWEPT_FACE",FACE,{"disambiguationData":[OSD([sQuery(id+"F7.wireOp",EDGE,"E67")])]})]});}
            var Q5;
            Q5=makeQuery(id+"F8.boolean.opBoolean","INTERSECT",EDGE,{"disambiguationData":[OD(0.0)],"derivedFrom":[makeQuery(id+"F5.opExtrude","SWEPT_FACE",FACE,{"disambiguationData":[OSD([sQuery(id+"F4.wireOp",EDGE,"E30")])]}),makeQuery(id+"F8.opExtrude","SWEPT_FACE",FACE,{"disambiguationData":[OSD([sQuery(id+"F7.wireOp",EDGE,"E67")])]})]});
            fillet(context, id + "F14", {"entities" : qUnion([Q0, Q1, Q2, Q3, Q4, Q5]), "radius" : 3 * mm, "tangentPropagation" : true, "allowEdgeOverflow" : false});
        }
        {
            var Q0;
            Q0=makeQuery(id+"F1.opExtrude","CAP_EDGE",EDGE,{"disambiguationData":[OSD([sQuery(id+"F0.wireOp",EDGE,"E1.bottom")])],"isStart":false});
            fillet(context, id + "F15", {"entities" : qUnion([Q0]), "radius" : 2 * mm, "tangentPropagation" : true, "allowEdgeOverflow" : false});
        }
        {
            var Q0;
            {var subQ0=sQuery(id+"F0.wireOp",EDGE,"E21.filletArc");var subQ1=sQuery(id+"F0.wireOp",EDGE,"E7");var subQ2=sQuery(id+"F0.wireOp",EDGE,"E6");var subQ3=sQuery(id+"F0.wireOp",EDGE,"E5");var subQ4=sQuery(id+"F0.wireOp",EDGE,"E4");var subQ5=sQuery(id+"F0.wireOp",EDGE,"E22.filletArc");var subQ6=sQuery(id+"F0.wireOp",EDGE,"E1.bottom");var subQ7=sQuery(id+"F0.wireOp",EDGE,"E1.right");var subQ8=sQuery(id+"F0.wireOp",EDGE,"E1.top");var subQ9=sQuery(id+"F0.wireOp",EDGE,"E1.left");var subQ10=sQuery(id+"F0.wireOp",EDGE,"E23.filletArc");var subQ11=sQuery(id+"F0.wireOp",EDGE,"E24.filletArc");Q0=makeQuery(id+"F2.boolean.opBoolean","SPLIT",FACE,{"disambiguationData":[TD([makeQuery(id+"F1.opExtrude","SWEPT_FACE",FACE,{"disambiguationData":[OSD([subQ6])]})])],"derivedFrom":makeQuery(id+"F1.opExtrude","CAP_FACE",FACE,{"disambiguationData":[OSD([subQ6,subQ8,subQ9,subQ7,subQ4,subQ3,subQ2,subQ1,subQ0,subQ5,subQ10,subQ11])],"isStart":true})});}
            var sketch = newSketch(context, id + "F16", { "sketchPlane" : qUnion([Q0])});
            skLineSegment(sketch, "E79.1", {"start": v(-70, 90) * mm, "end": v(70, 90) * mm});
            skArc(sketch, "E79.2", {"start": v(80, 80) * mm, "mid": v(77.07, 87.07) * mm, "end": v(70, 90) * mm});
            skLineSegment(sketch, "E79.3", {"start": v(80, -80) * mm, "end": v(80, 80) * mm});
            skArc(sketch, "E79.4", {"start": v(70, -90) * mm, "mid": v(77.07, -87.07) * mm, "end": v(80, -80) * mm});
            skLineSegment(sketch, "E79.5", {"start": v(-70, -90) * mm, "end": v(70, -90) * mm});
            skLineSegment(sketch, "E79.6", {"start": v(-80, -80) * mm, "end": v(-80, 80) * mm});
            skArc(sketch, "E79.7", {"start": v(-80, -80) * mm, "mid": v(-77.07, -87.07) * mm, "end": v(-70, -90) * mm});
            skArc(sketch, "E79.8", {"start": v(-70, 90) * mm, "mid": v(-77.07, 87.07) * mm, "end": v(-80, 80) * mm});
            skCircle(sketch, "E80.8", {"center": v(-60, 67.5) * mm, "radius": 4 * mm});
            skCircle(sketch, "E80.9", {"center": v(-60, -67.5) * mm, "radius": 4 * mm});
            skCircle(sketch, "E80.10", {"center": v(60, -67.5) * mm, "radius": 4 * mm});
            skCircle(sketch, "E80.11", {"center": v(60, 67.5) * mm, "radius": 4 * mm});
            skArc(sketch, "E80.12", {"start": v(56.15, 48.18) * mm, "mid": v(0, 67.5) * mm, "end": v(-56.15, 48.18) * mm});
            skArc(sketch, "E80.13", {"start": v(60, 40.3) * mm, "mid": v(58.99, 44.68) * mm, "end": v(56.15, 48.18) * mm});
            skLineSegment(sketch, "E80.14", {"start": v(60, 40.3) * mm, "end": v(60, -40.3) * mm});
            skArc(sketch, "E80.15", {"start": v(56.15, -48.18) * mm, "mid": v(58.99, -44.68) * mm, "end": v(60, -40.3) * mm});
            skArc(sketch, "E80.16", {"start": v(-56.15, -48.18) * mm, "mid": v(0, -67.5) * mm, "end": v(56.15, -48.18) * mm});
            skLineSegment(sketch, "E80.17", {"start": v(-60, 40.3) * mm, "end": v(-60, -40.3) * mm});
            skArc(sketch, "E80.18", {"start": v(-60, -40.3) * mm, "mid": v(-58.99, -44.68) * mm, "end": v(-56.15, -48.18) * mm});
            skArc(sketch, "E80.19", {"start": v(-56.15, 48.18) * mm, "mid": v(-58.99, 44.68) * mm, "end": v(-60, 40.3) * mm});
            skLineSegment(sketch, "E81", {"start": v(0, 90) * mm, "end": v(0, 120) * mm, "construction": true});
            skCircle(sketch, "E82", {"center": v(0, 120) * mm, "radius": 6 * mm});
            skLineSegment(sketch, "E83", {"start": v(-33, 90) * mm, "end": v(-15, 108) * mm});
            skLineSegment(sketch, "E84", {"start": v(33, 90) * mm, "end": v(15, 108) * mm});
            skLineSegment(sketch, "E85", {"start": v(15, 108) * mm, "end": v(15, 120) * mm});
            skLineSegment(sketch, "E86", {"start": v(-15, 108) * mm, "end": v(-15, 120) * mm});
            skArc(sketch, "E87", {"start": v(15, 120) * mm, "mid": v(0, 135) * mm, "end": v(-15, 120) * mm});
            skLineSegment(sketch, "E88", {"start": v(-80, 0) * mm, "end": v(80, 0) * mm, "construction": true});
            skLineSegment(sketch, "E89.MirrorCS", {"start": v(-15, -108) * mm, "end": v(-15, -120) * mm});
            skLineSegment(sketch, "E90.MirrorCS", {"start": v(-33, -90) * mm, "end": v(-15, -108) * mm});
            skArc(sketch, "E91.MirrorCS", {"start": v(15, -120) * mm, "mid": v(0, -135) * mm, "end": v(-15, -120) * mm});
            skLineSegment(sketch, "E92.MirrorCS", {"start": v(15, -108) * mm, "end": v(15, -120) * mm});
            skLineSegment(sketch, "E93.MirrorCS", {"start": v(33, -90) * mm, "end": v(15, -108) * mm});
            skLineSegment(sketch, "E94.MirrorCS", {"start": v(0, -90) * mm, "end": v(0, -120) * mm, "construction": true});
            skCircle(sketch, "E95.MirrorC", {"center": v(0, -120) * mm, "radius": 6 * mm});
            skSolve(sketch);
        }
        {
            var Q0;
            Q0 = qSketchRegion(id + "F16", true);
            var Q1;
            Q1=makeQuery(id+"F2.opExtrude","CAP_FACE",FACE,{"disambiguationData":[OSD([sQuery(id+"F0.wireOp",EDGE,"E12"),sQuery(id+"F0.wireOp",EDGE,"E13"),sQuery(id+"F0.wireOp",EDGE,"E14"),sQuery(id+"F0.wireOp",EDGE,"E15"),sQuery(id+"F0.wireOp",EDGE,"E17.filletArc"),sQuery(id+"F0.wireOp",EDGE,"E18.filletArc"),sQuery(id+"F0.wireOp",EDGE,"E19.filletArc"),sQuery(id+"F0.wireOp",EDGE,"E20.filletArc"),sQuery(id+"F0.wireOp",EDGE,"E25.0"),sQuery(id+"F0.wireOp",EDGE,"E25.1"),sQuery(id+"F0.wireOp",EDGE,"E25.2"),sQuery(id+"F0.wireOp",EDGE,"E25.3"),sQuery(id+"F0.wireOp",EDGE,"E25.4"),sQuery(id+"F0.wireOp",EDGE,"E25.5"),sQuery(id+"F0.wireOp",EDGE,"E25.6"),sQuery(id+"F0.wireOp",EDGE,"E25.7")])],"isStart":false});
            extrude(context, id + "F17", {"entities" : qUnion([Q0]), "endBound" : BoundingType.UP_TO_SURFACE, "depth" : 25 * mm, "endBoundEntityFace" : qUnion([Q1]), "offsetDistance" : 25 * mm});
        }
    });
